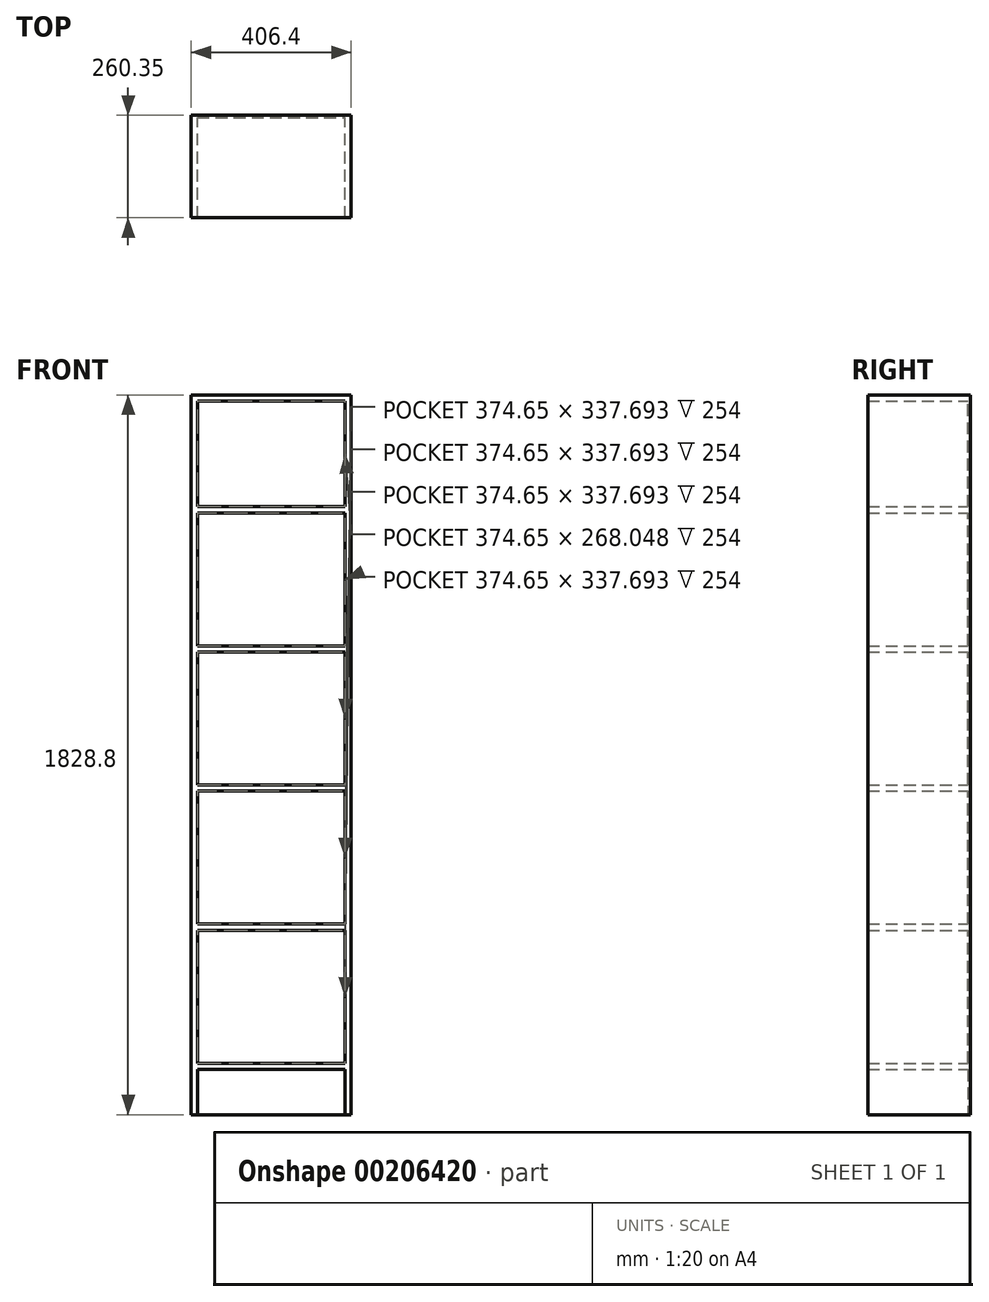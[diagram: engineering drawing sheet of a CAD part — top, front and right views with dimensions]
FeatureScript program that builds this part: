
annotation { "Feature Type Name" : "Feature", "Feature Type Description" : "" }
export const myFeature = defineFeature(function(context is Context, id is Id, definition is map)
    precondition{}
    {
        {
            var Q0;
            Q0=qCreatedBy(makeId("Front.planeOp"),FACE);
            var sketch = newSketch(context, id + "F0", { "sketchPlane" : qUnion([Q0])});
            skLineSegment(sketch, "E0.bottom", {"start": v(0, 0) * mm, "end": v(-15.88, 0) * mm});
            skLineSegment(sketch, "E0.top", {"start": v(0, 1828.8) * mm, "end": v(-15.88, 1828.8) * mm});
            skLineSegment(sketch, "E0.left", {"start": v(0, 0) * mm, "end": v(0, 1828.8) * mm});
            skLineSegment(sketch, "E0.right", {"start": v(-15.88, 0) * mm, "end": v(-15.88, 114.73) * mm});
            skLineSegment(sketch, "E1.bottom", {"start": v(-15.88, 1828.8) * mm, "end": v(-390.53, 1828.8) * mm});
            skLineSegment(sketch, "E1.top", {"start": v(-15.88, 1812.93) * mm, "end": v(-390.53, 1812.93) * mm});
            skLineSegment(sketch, "E2.bottom", {"start": v(-390.53, 1828.8) * mm, "end": v(-406.4, 1828.8) * mm});
            skLineSegment(sketch, "E2.top", {"start": v(-390.53, 0) * mm, "end": v(-406.4, 0) * mm});
            skLineSegment(sketch, "E2.left", {"start": v(-390.53, 1812.93) * mm, "end": v(-390.53, 1544.88) * mm});
            skLineSegment(sketch, "E2.right", {"start": v(-406.4, 1828.8) * mm, "end": v(-406.4, 0) * mm});
            skLineSegment(sketch, "E3.bottom", {"start": v(-390.53, 114.73) * mm, "end": v(-15.88, 114.73) * mm});
            skLineSegment(sketch, "E3.top", {"start": v(-390.53, 130.6) * mm, "end": v(-15.88, 130.6) * mm});
            skLineSegment(sketch, "E4.0.1.0", {"start": v(-390.52, 468.3) * mm, "end": v(-15.88, 468.3) * mm});
            skLineSegment(sketch, "E4.0.1.1", {"start": v(-390.52, 484.17) * mm, "end": v(-15.88, 484.17) * mm});
            skLineSegment(sketch, "E4.0.2.0", {"start": v(-390.53, 821.87) * mm, "end": v(-15.88, 821.87) * mm});
            skLineSegment(sketch, "E4.0.2.1", {"start": v(-390.53, 837.74) * mm, "end": v(-15.88, 837.74) * mm});
            skLineSegment(sketch, "E4.0.3.0", {"start": v(-390.53, 1175.43) * mm, "end": v(-15.88, 1175.43) * mm});
            skLineSegment(sketch, "E4.0.3.1", {"start": v(-390.53, 1191.3) * mm, "end": v(-15.88, 1191.3) * mm});
            skLineSegment(sketch, "E4.0.4.0", {"start": v(-390.53, 1529) * mm, "end": v(-15.88, 1529) * mm});
            skLineSegment(sketch, "E4.0.4.1", {"start": v(-390.53, 1544.88) * mm, "end": v(-15.88, 1544.88) * mm});
            skLineSegment(sketch, "E4.direction1", {"start": v(-390.53, 114.73) * mm, "end": v(-365.52, 114.73) * mm, "construction": true});
            skLineSegment(sketch, "E4.direction2", {"start": v(-390.52, 130.6) * mm, "end": v(-390.52, 468.3) * mm, "construction": true});
            skLineSegment(sketch, "E5.trimOffspring", {"start": v(-15.88, 484.17) * mm, "end": v(-15.88, 821.87) * mm});
            skLineSegment(sketch, "E6.trimOffspring", {"start": v(-15.88, 130.6) * mm, "end": v(-15.88, 468.3) * mm});
            skLineSegment(sketch, "E7.trimOffspring", {"start": v(-390.53, 114.73) * mm, "end": v(-390.53, 0) * mm});
            skLineSegment(sketch, "E8.trimOffspring", {"start": v(-390.53, 468.3) * mm, "end": v(-390.53, 130.6) * mm});
            skLineSegment(sketch, "E9.trimOffspring", {"start": v(-390.53, 821.87) * mm, "end": v(-390.53, 484.17) * mm});
            skLineSegment(sketch, "E10.trimOffspring", {"start": v(-15.88, 837.74) * mm, "end": v(-15.88, 1175.43) * mm});
            skLineSegment(sketch, "E11.trimOffspring", {"start": v(-15.88, 1191.3) * mm, "end": v(-15.88, 1529) * mm});
            skLineSegment(sketch, "E12.trimOffspring", {"start": v(-390.53, 1175.43) * mm, "end": v(-390.53, 837.74) * mm});
            skLineSegment(sketch, "E13.trimOffspring", {"start": v(-15.88, 1544.88) * mm, "end": v(-15.88, 1812.93) * mm});
            skLineSegment(sketch, "E14.trimOffspring", {"start": v(-390.53, 1529) * mm, "end": v(-390.53, 1191.3) * mm});
            skSolve(sketch);
        }
        {
            var Q0;
            Q0=makeQuery(id+"F0.imprint","IMPRINT",FACE,{"disambiguationData":[TD([[makeQuery(id+"F0.imprint","IMPRINT",EDGE,{"derivedFrom":sQuery(id+"F0.wireOp",EDGE,"E0.bottom")}),-1.0]])]});
            extrude(context, id + "F1", {"entities" : qUnion([Q0]), "depth" : 254 * mm});
        }
        {
            var Q0;
            Q0=makeQuery(id+"F1.opExtrude","CAP_FACE",FACE,{"disambiguationData":[OSD([sQuery(id+"F0.wireOp",EDGE,"E0.bottom"),sQuery(id+"F0.wireOp",EDGE,"E0.top"),sQuery(id+"F0.wireOp",EDGE,"E0.left"),sQuery(id+"F0.wireOp",EDGE,"E0.right"),sQuery(id+"F0.wireOp",EDGE,"E1.bottom"),sQuery(id+"F0.wireOp",EDGE,"E1.top"),sQuery(id+"F0.wireOp",EDGE,"E2.bottom"),sQuery(id+"F0.wireOp",EDGE,"E2.top"),sQuery(id+"F0.wireOp",EDGE,"E2.left"),sQuery(id+"F0.wireOp",EDGE,"E2.right"),sQuery(id+"F0.wireOp",EDGE,"E3.bottom"),sQuery(id+"F0.wireOp",EDGE,"E3.top"),sQuery(id+"F0.wireOp",EDGE,"E4.0.1.0"),sQuery(id+"F0.wireOp",EDGE,"E4.0.1.1"),sQuery(id+"F0.wireOp",EDGE,"E4.0.2.0"),sQuery(id+"F0.wireOp",EDGE,"E4.0.2.1"),sQuery(id+"F0.wireOp",EDGE,"E4.0.3.0"),sQuery(id+"F0.wireOp",EDGE,"E4.0.3.1"),sQuery(id+"F0.wireOp",EDGE,"E4.0.4.0"),sQuery(id+"F0.wireOp",EDGE,"E4.0.4.1"),sQuery(id+"F0.wireOp",EDGE,"E5.trimOffspring"),sQuery(id+"F0.wireOp",EDGE,"E6.trimOffspring"),sQuery(id+"F0.wireOp",EDGE,"E7.trimOffspring"),sQuery(id+"F0.wireOp",EDGE,"E8.trimOffspring"),sQuery(id+"F0.wireOp",EDGE,"E9.trimOffspring"),sQuery(id+"F0.wireOp",EDGE,"E10.trimOffspring"),sQuery(id+"F0.wireOp",EDGE,"E11.trimOffspring"),sQuery(id+"F0.wireOp",EDGE,"E12.trimOffspring"),sQuery(id+"F0.wireOp",EDGE,"E13.trimOffspring"),sQuery(id+"F0.wireOp",EDGE,"E14.trimOffspring")])],"isStart":true});
            var sketch = newSketch(context, id + "F2", { "sketchPlane" : qUnion([Q0])});
            skLineSegment(sketch, "E15.bottom", {"start": v(406.4, 0) * mm, "end": v(0, 0) * mm});
            skLineSegment(sketch, "E15.top", {"start": v(406.4, 1828.8) * mm, "end": v(0, 1828.8) * mm});
            skLineSegment(sketch, "E15.left", {"start": v(406.4, 0) * mm, "end": v(406.4, 1828.8) * mm});
            skLineSegment(sketch, "E15.right", {"start": v(0, 0) * mm, "end": v(0, 1828.8) * mm});
            skSolve(sketch);
        }
        {
            var Q0;
            Q0 = qSketchRegion(id + "F2", true);
            extrude(context, id + "F3", {"entities" : qUnion([Q0]), "operationType" : NewBodyOperationType.ADD, "depth" : 6.35 * mm});
        }
    });
